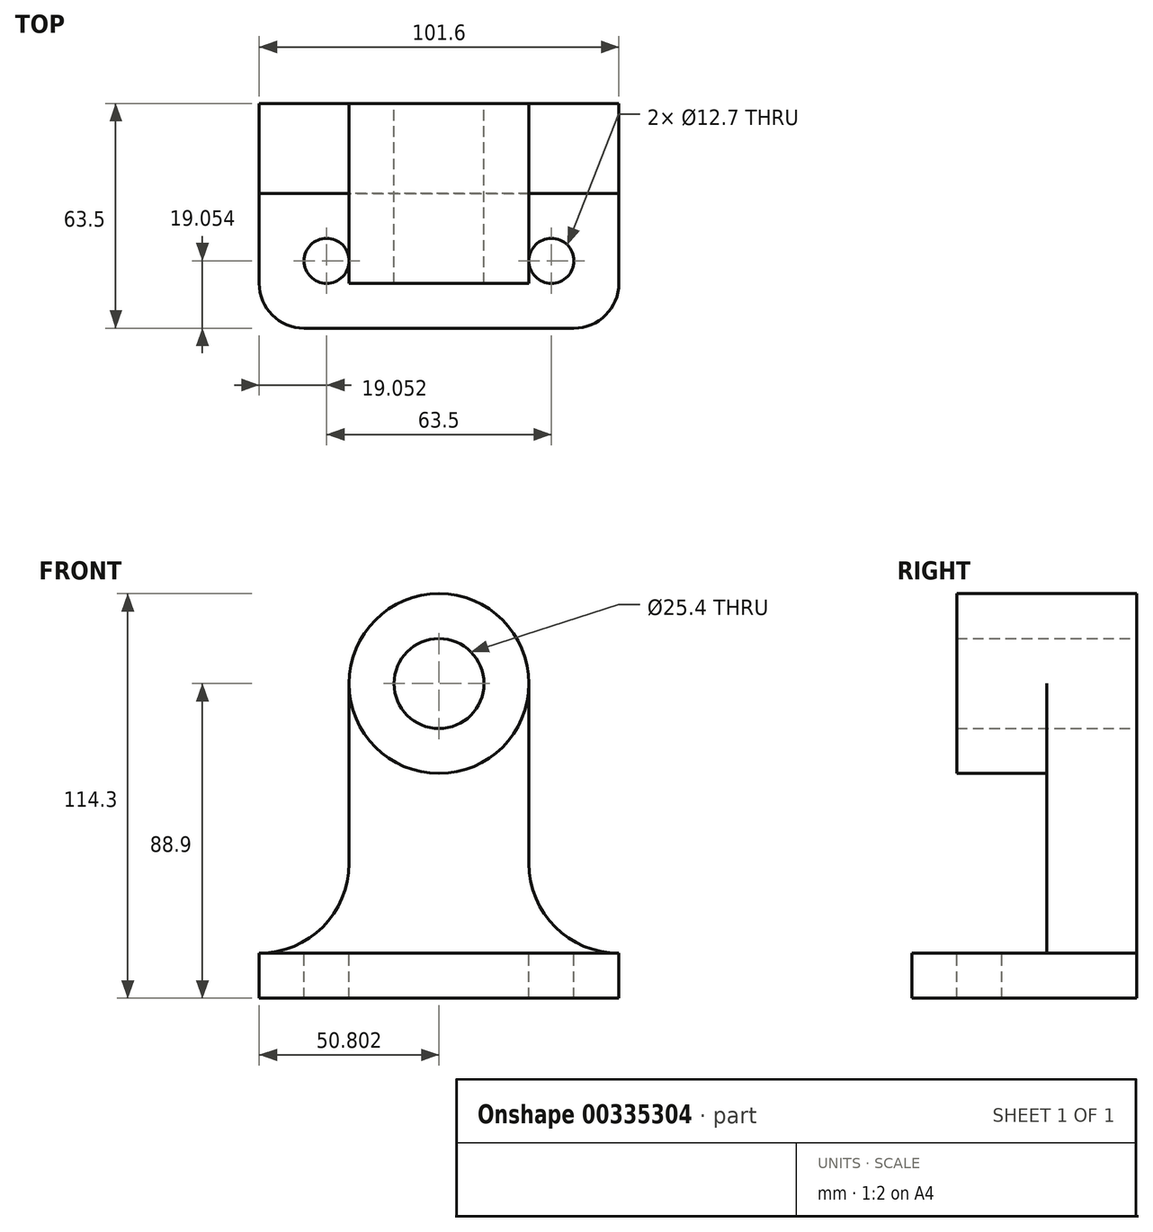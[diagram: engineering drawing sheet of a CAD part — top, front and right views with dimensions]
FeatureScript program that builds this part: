
annotation { "Feature Type Name" : "Feature", "Feature Type Description" : "" }
export const myFeature = defineFeature(function(context is Context, id is Id, definition is map)
    precondition{}
    {
        {
            var Q0;
            Q0=qCreatedBy(makeId("Top.planeOp"),FACE);
            var sketch = newSketch(context, id + "F0", { "sketchPlane" : qUnion([Q0])});
            skLineSegment(sketch, "E0.bottom", {"start": v(-45.58, 38.58) * mm, "end": v(56.02, 38.58) * mm});
            skLineSegment(sketch, "E0.top", {"start": v(-32.88, -24.92) * mm, "end": v(43.32, -24.92) * mm});
            skLineSegment(sketch, "E0.left", {"start": v(-45.58, 38.58) * mm, "end": v(-45.58, -12.22) * mm});
            skLineSegment(sketch, "E0.right", {"start": v(56.02, 38.58) * mm, "end": v(56.02, -12.22) * mm});
            skPoint(sketch, "E1.visualSharp", {"position": v(-45.58, -24.92) * mm});
            skArc(sketch, "E1.filletArc", {"start": v(-45.58, -12.22) * mm, "mid": v(-41.86, -21.2) * mm, "end": v(-32.88, -24.92) * mm});
            skPoint(sketch, "E2.visualSharp", {"position": v(56.02, -24.92) * mm});
            skArc(sketch, "E2.filletArc", {"start": v(43.32, -24.92) * mm, "mid": v(52.3, -21.2) * mm, "end": v(56.02, -12.22) * mm});
            skSolve(sketch);
        }
        {
            var Q0;
            Q0=makeQuery(id+"F0.imprint","IMPRINT",FACE,{"disambiguationData":[TD([[makeQuery(id+"F0.imprint","IMPRINT",EDGE,{"derivedFrom":sQuery(id+"F0.wireOp",EDGE,"E0.bottom")}),-1.0]])]});
            extrude(context, id + "F1", {"entities" : qUnion([Q0]), "depth" : 12.7 * mm});
        }
        {
            var Q0;
            Q0=makeQuery(id+"F1.opExtrude","CAP_FACE",FACE,{"disambiguationData":[OSD([sQuery(id+"F0.wireOp",EDGE,"E0.bottom"),sQuery(id+"F0.wireOp",EDGE,"E0.top"),sQuery(id+"F0.wireOp",EDGE,"E0.left"),sQuery(id+"F0.wireOp",EDGE,"E0.right"),sQuery(id+"F0.wireOp",EDGE,"E1.filletArc"),sQuery(id+"F0.wireOp",EDGE,"E2.filletArc")])],"isStart":false});
            var sketch = newSketch(context, id + "F2", { "sketchPlane" : qUnion([Q0])});
            skCircle(sketch, "E3", {"center": v(-26.53, -5.87) * mm, "radius": 6.35 * mm});
            skCircle(sketch, "E4", {"center": v(36.97, -5.87) * mm, "radius": 6.35 * mm});
            skSolve(sketch);
        }
        {
            var Q0;
            Q0=makeQuery(id+"F2.imprint","IMPRINT",FACE,{"disambiguationData":[TD([[makeQuery(id+"F2.imprint","IMPRINT",EDGE,{"derivedFrom":sQuery(id+"F2.wireOp",EDGE,"E3")}),1.0]])]});
            var Q1;
            Q1=makeQuery(id+"F2.imprint","IMPRINT",FACE,{"disambiguationData":[TD([[makeQuery(id+"F2.imprint","IMPRINT",EDGE,{"derivedFrom":sQuery(id+"F2.wireOp",EDGE,"E4")}),1.0]])]});
            extrude(context, id + "F3", {"entities" : qUnion([Q0, Q1]), "operationType" : NewBodyOperationType.REMOVE, "oppositeDirection" : true, "depth" : 12.7 * mm});
        }
        {
            var Q0;
            Q0=makeQuery(id+"F1.opExtrude","SWEPT_FACE",FACE,{"disambiguationData":[OSD([sQuery(id+"F0.wireOp",EDGE,"E0.bottom")])]});
            var sketch = newSketch(context, id + "F4", { "sketchPlane" : qUnion([Q0])});
            skLineSegment(sketch, "E5", {"start": v(-30.62, 38.1) * mm, "end": v(-30.62, 88.9) * mm});
            skLineSegment(sketch, "E6", {"start": v(20.18, 88.9) * mm, "end": v(20.18, 38.1) * mm});
            skArc(sketch, "E7", {"start": v(20.18, 88.9) * mm, "mid": v(-5.22, 114.3) * mm, "end": v(-30.62, 88.9) * mm});
            skArc(sketch, "E8", {"start": v(-56.02, 12.7) * mm, "mid": v(-38.06, 20.14) * mm, "end": v(-30.62, 38.1) * mm});
            skArc(sketch, "E9", {"start": v(20.18, 38.1) * mm, "mid": v(27.62, 20.14) * mm, "end": v(45.58, 12.7) * mm});
            skLineSegment(sketch, "E10", {"start": v(-30.62, 12.7) * mm, "end": v(-56.02, 12.7) * mm});
            skLineSegment(sketch, "E11", {"start": v(45.58, 12.7) * mm, "end": v(20.18, 12.7) * mm});
            skSolve(sketch);
        }
        {
            var Q0;
            Q0=makeQuery(id+"F4.imprint","IMPRINT",FACE,{"disambiguationData":[TD([[makeQuery(id+"F4.imprint","IMPRINT",EDGE,{"derivedFrom":sQuery(id+"F4.wireOp",EDGE,"E5")}),-1.0]])]});
            extrude(context, id + "F5", {"entities" : qUnion([Q0]), "operationType" : NewBodyOperationType.ADD, "oppositeDirection" : true, "depth" : 25.4 * mm});
        }
        {
            var Q0;
            Q0=makeQuery(id+"F5.opExtrude","CAP_FACE",FACE,{"disambiguationData":[OSD([sQuery(id+"F0.wireOp",EDGE,"E0.bottom"),sQuery(id+"F4.wireOp",EDGE,"E5"),sQuery(id+"F4.wireOp",EDGE,"E6"),sQuery(id+"F4.wireOp",EDGE,"E7"),sQuery(id+"F4.wireOp",EDGE,"E8"),sQuery(id+"F4.wireOp",EDGE,"E9"),sQuery(id+"F4.wireOp",EDGE,"E10"),sQuery(id+"F4.wireOp",EDGE,"E11")])],"isStart":false});
            var sketch = newSketch(context, id + "F6", { "sketchPlane" : qUnion([Q0])});
            skCircle(sketch, "E12", {"center": v(5.22, 88.9) * mm, "radius": 12.7 * mm});
            skCircle(sketch, "E13", {"center": v(5.22, 88.9) * mm, "radius": 25.4 * mm});
            skPoint(sketch, "E14.orphan", {"position": v(5.22, 114.3) * mm});
            skSolve(sketch);
        }
        {
            var Q0;
            Q0=makeQuery(id+"F6.imprint","IMPRINT",FACE,{"disambiguationData":[TD([[makeQuery(id+"F6.imprint","IMPRINT",EDGE,{"derivedFrom":sQuery(id+"F6.wireOp",EDGE,"E12")}),-1.0]])]});
            extrude(context, id + "F7", {"entities" : qUnion([Q0]), "operationType" : NewBodyOperationType.ADD, "depth" : 25.4 * mm});
        }
        {
            var Q0;
            Q0=makeQuery(id+"F7.boolean.opBoolean","SPLIT",FACE,{"disambiguationData":[TD([makeQuery(id+"F7.opExtrude","SWEPT_FACE",FACE,{"disambiguationData":[OSD([sQuery(id+"F6.wireOp",EDGE,"E12")])]})])],"derivedFrom":makeQuery(id+"F5.opExtrude","CAP_FACE",FACE,{"disambiguationData":[OSD([sQuery(id+"F0.wireOp",EDGE,"E0.bottom"),sQuery(id+"F4.wireOp",EDGE,"E5"),sQuery(id+"F4.wireOp",EDGE,"E6"),sQuery(id+"F4.wireOp",EDGE,"E7"),sQuery(id+"F4.wireOp",EDGE,"E8"),sQuery(id+"F4.wireOp",EDGE,"E9"),sQuery(id+"F4.wireOp",EDGE,"E10"),sQuery(id+"F4.wireOp",EDGE,"E11")])],"isStart":false})});
            extrude(context, id + "F8", {"entities" : qUnion([Q0]), "operationType" : NewBodyOperationType.REMOVE, "oppositeDirection" : true, "depth" : 25.4 * mm});
        }
    });
